# Revit family: 185-19-0.5
name_source: partatom
category: Aparatos sanitarios
units: mm (PartAtom-declared; Revit-internal decimal feet)

## family parameters
Compartido = Sí
Corte con vacíos al cargar = No
Cota de conector redondo = Diámetro de uso
Número OmniClass = 23.45.00.00
Punto de cálculo de habitación = No
Se basa en plano de trabajo = No
Siempre vertical = Sí
Tipo de pieza = Normal
Título OmniClass = Sanitary, Laundry, and Cleaning Equipment

## types (1)
- 185-19-0.5
    Certification = http://www.helvex.com.mx
    Chrome = Brass Chromed
    Comentarios de tipo = Flush Valves
    Compliance = NOM-005-CONAGUA-1996
    Conexión AF = Sí
    Connection = 1" Feeding Connection
    Descripción = Exposed Urinal Flush Vlave With Lever
    Documentation = http://www.helvex.com.mx
    Elevación por defecto = 0"
    Fabricante = HELVEX
    Features = Lever With Antibacterial Coating, Left Or Right Connection
    Flow = 0.5 Lts Per Flush
    Max. Working Pressure = 85.3 psi
    Min. Working Pressure = 14.2 psi
    Modelo = 185-19-0.5
    Note = Feeding Pipe Must Be 1 ¼" And Connect a  ¼" - 1" Reductor to Stop Valve
    URL = http://www.helvex.com.mx

## geometry (parser evidence)
native form markers: Sweep x3
no freeform markers — native parametric forms only
